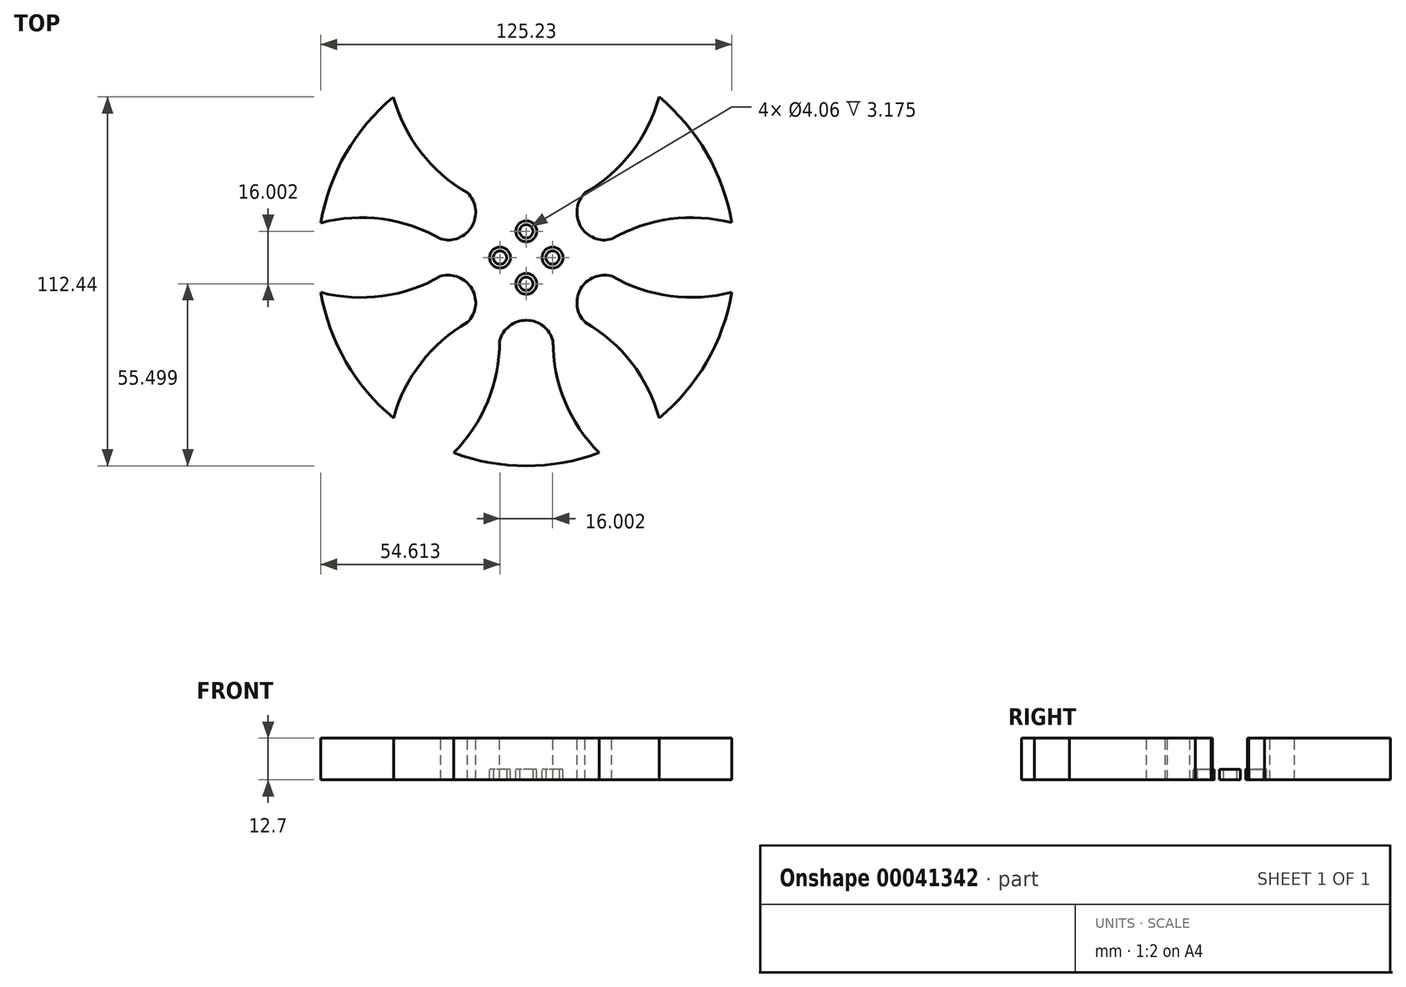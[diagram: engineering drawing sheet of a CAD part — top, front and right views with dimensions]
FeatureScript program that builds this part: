
annotation { "Feature Type Name" : "Feature", "Feature Type Description" : "" }
export const myFeature = defineFeature(function(context is Context, id is Id, definition is map)
    precondition{}
    {
        {
            var Q0;
            Q0=qCreatedBy(makeId("Top.planeOp"),FACE);
            var sketch = newSketch(context, id + "F0", { "sketchPlane" : qUnion([Q0])});
            skCircle(sketch, "E0", {"center": v(-620.67, 147.96) * mm, "radius": 63.5 * mm});
            skCircle(sketch, "E1", {"center": v(-620.67, 147.96) * mm, "radius": 4.06 * mm});
            skCircle(sketch, "E2", {"center": v(-612.66, 147.96) * mm, "radius": 2.03 * mm});
            skCircle(sketch, "E3", {"center": v(-620.67, 155.96) * mm, "radius": 2.03 * mm});
            skCircle(sketch, "E4", {"center": v(-628.67, 147.96) * mm, "radius": 2.03 * mm});
            skCircle(sketch, "E5", {"center": v(-620.67, 139.96) * mm, "radius": 2.03 * mm});
            skCircle(sketch, "E6", {"center": v(-620.67, 147.96) * mm, "radius": 25.4 * mm});
            skSolve(sketch);
        }
        {
            var Q0;
            Q0=makeQuery(id+"F0.imprint","IMPRINT",FACE,{"disambiguationData":[TD([[makeQuery(id+"F0.imprint","IMPRINT",EDGE,{"derivedFrom":sQuery(id+"F0.wireOp",EDGE,"E0")}),1.0]])]});
            var Q1;
            Q1=makeQuery(id+"F0.imprint","IMPRINT",FACE,{"disambiguationData":[TD([[makeQuery(id+"F0.imprint","IMPRINT",EDGE,{"derivedFrom":sQuery(id+"F0.wireOp",EDGE,"E1")}),-1.0]])]});
            extrude(context, id + "F1", {"entities" : qUnion([Q0, Q1]), "depth" : 12.7 * mm});
        }
        {
            var Q0;
            Q0=makeQuery(id+"F1.opExtrude","CAP_FACE",FACE,{"disambiguationData":[OSD([sQuery(id+"F0.wireOp",EDGE,"E0"),sQuery(id+"F0.wireOp",EDGE,"E1"),sQuery(id+"F0.wireOp",EDGE,"E2"),sQuery(id+"F0.wireOp",EDGE,"E3"),sQuery(id+"F0.wireOp",EDGE,"E4"),sQuery(id+"F0.wireOp",EDGE,"E5")])],"isStart":false});
            var sketch = newSketch(context, id + "F2", { "sketchPlane" : qUnion([Q0])});
            skCircle(sketch, "E7", {"center": v(-620.67, 155.96) * mm, "radius": 3.18 * mm});
            skCircle(sketch, "E8", {"center": v(-612.66, 147.96) * mm, "radius": 3.18 * mm});
            skCircle(sketch, "E9", {"center": v(-620.67, 139.96) * mm, "radius": 3.18 * mm});
            skCircle(sketch, "E10", {"center": v(-628.67, 147.96) * mm, "radius": 3.18 * mm});
            skLineSegment(sketch, "E11", {"start": v(-620.67, 155.96) * mm, "end": v(-620.67, 167.07) * mm});
            skArc(sketch, "E12", {"start": v(-598.54, 207.48) * mm, "mid": v(-608.9, 191.8) * mm, "end": v(-612.54, 173.36) * mm});
            skArc(sketch, "E13.MirrorCS", {"start": v(-642.82, 207.47) * mm, "mid": v(-632.44, 191.8) * mm, "end": v(-628.8, 173.36) * mm});
            skArc(sketch, "E14", {"start": v(-628.8, 173.36) * mm, "mid": v(-620.67, 167.07) * mm, "end": v(-612.54, 173.36) * mm});
            skPoint(sketch, "E15.orphan", {"position": v(-620.67, 211.46) * mm});
            skPoint(sketch, "E16.trimOffspring.start.orphan", {"position": v(-620.67, 173.36) * mm});
            skArc(sketch, "E17.1.0", {"start": v(-683.28, 158.53) * mm, "mid": v(-664.52, 159.69) * mm, "end": v(-646.73, 153.62) * mm});
            skArc(sketch, "E17.1.1", {"start": v(-646.73, 153.62) * mm, "mid": v(-637.21, 157.51) * mm, "end": v(-638.6, 167.7) * mm});
            skArc(sketch, "E17.1.2", {"start": v(-661.15, 196.88) * mm, "mid": v(-652.76, 180.06) * mm, "end": v(-638.6, 167.7) * mm});
            skArc(sketch, "E17.2.0", {"start": v(-661.12, 99.02) * mm, "mid": v(-652.75, 115.84) * mm, "end": v(-638.6, 128.22) * mm});
            skArc(sketch, "E17.2.1", {"start": v(-638.6, 128.22) * mm, "mid": v(-637.21, 138.4) * mm, "end": v(-646.73, 142.3) * mm});
            skArc(sketch, "E17.2.2", {"start": v(-683.28, 137.36) * mm, "mid": v(-664.51, 136.22) * mm, "end": v(-646.73, 142.3) * mm});
            skArc(sketch, "E17.3.0", {"start": v(-598.51, 88.45) * mm, "mid": v(-608.9, 104.12) * mm, "end": v(-612.54, 122.56) * mm});
            skArc(sketch, "E17.3.1", {"start": v(-612.54, 122.56) * mm, "mid": v(-620.67, 128.85) * mm, "end": v(-628.8, 122.56) * mm});
            skArc(sketch, "E17.3.2", {"start": v(-642.8, 88.44) * mm, "mid": v(-632.42, 104.12) * mm, "end": v(-628.8, 122.56) * mm});
            skArc(sketch, "E17.4.0", {"start": v(-558.05, 137.4) * mm, "mid": v(-576.81, 136.23) * mm, "end": v(-594.6, 142.3) * mm});
            skArc(sketch, "E17.4.1", {"start": v(-594.6, 142.3) * mm, "mid": v(-604.12, 138.4) * mm, "end": v(-602.73, 128.22) * mm});
            skArc(sketch, "E17.4.2", {"start": v(-580.18, 99.04) * mm, "mid": v(-588.58, 115.86) * mm, "end": v(-602.73, 128.22) * mm});
            skArc(sketch, "E17.5.0", {"start": v(-580.2, 196.9) * mm, "mid": v(-588.58, 180.07) * mm, "end": v(-602.73, 167.7) * mm});
            skArc(sketch, "E17.5.1", {"start": v(-602.73, 167.7) * mm, "mid": v(-604.12, 157.51) * mm, "end": v(-594.6, 153.62) * mm});
            skArc(sketch, "E17.5.2", {"start": v(-558.06, 158.56) * mm, "mid": v(-576.82, 159.7) * mm, "end": v(-594.6, 153.62) * mm});
            skPoint(sketch, "E17.center", {"position": v(-620.67, 147.96) * mm});
            skSolve(sketch);
        }
        {
            var Q0;
            Q0=makeQuery(id+"F2.imprint","IMPRINT",FACE,{"disambiguationData":[TD([[makeQuery(id+"F2.imprint","IMPRINT",EDGE,{"derivedFrom":sQuery(id+"F2.wireOp",EDGE,"E10")}),1.0]])]});
            var Q1;
            Q1=makeQuery(id+"F2.imprint","IMPRINT",FACE,{"disambiguationData":[TD([[makeQuery(id+"F2.imprint","IMPRINT",EDGE,{"derivedFrom":sQuery(id+"F2.wireOp",EDGE,"E7")}),1.0]])]});
            var Q2;
            Q2=makeQuery(id+"F2.imprint","IMPRINT",FACE,{"disambiguationData":[TD([[makeQuery(id+"F2.imprint","IMPRINT",EDGE,{"derivedFrom":sQuery(id+"F2.wireOp",EDGE,"E8")}),1.0]])]});
            var Q3;
            Q3=makeQuery(id+"F2.imprint","IMPRINT",FACE,{"disambiguationData":[TD([[makeQuery(id+"F2.imprint","IMPRINT",EDGE,{"derivedFrom":sQuery(id+"F2.wireOp",EDGE,"E9")}),1.0]])]});
            extrude(context, id + "F3", {"entities" : qUnion([Q0, Q1, Q2, Q3]), "operationType" : NewBodyOperationType.REMOVE, "oppositeDirection" : true, "depth" : 9.52 * mm});
        }
        {
            var Q0;
            {var subQ2=sQuery(id+"F2.wireOp",EDGE,"E12");Q0=makeQuery(id+"F2.imprint","IMPRINT",FACE,{"disambiguationData":[TD([[makeQuery(id+"F2.imprint","IMPRINT",EDGE,{"derivedFrom":subQ2}),-1.0]])]});}
            var Q1;
            {var subQ0=sQuery(id+"F2.wireOp",EDGE,"E17.1.0");Q1=makeQuery(id+"F2.imprint","IMPRINT",FACE,{"disambiguationData":[TD([[makeQuery(id+"F2.imprint","IMPRINT",EDGE,{"derivedFrom":subQ0}),1.0]])]});}
            var Q2;
            {var subQ0=sQuery(id+"F2.wireOp",EDGE,"E17.2.0");Q2=makeQuery(id+"F2.imprint","IMPRINT",FACE,{"disambiguationData":[TD([[makeQuery(id+"F2.imprint","IMPRINT",EDGE,{"derivedFrom":subQ0}),1.0]])]});}
            var Q3;
            {var subQ0=sQuery(id+"F2.wireOp",EDGE,"E17.3.0");Q3=makeQuery(id+"F2.imprint","IMPRINT",FACE,{"disambiguationData":[TD([[makeQuery(id+"F2.imprint","IMPRINT",EDGE,{"derivedFrom":subQ0}),1.0]])]});}
            var Q4;
            {var subQ0=sQuery(id+"F2.wireOp",EDGE,"E17.4.0");Q4=makeQuery(id+"F2.imprint","IMPRINT",FACE,{"disambiguationData":[TD([[makeQuery(id+"F2.imprint","IMPRINT",EDGE,{"derivedFrom":subQ0}),1.0]])]});}
            var Q5;
            {var subQ0=sQuery(id+"F2.wireOp",EDGE,"E17.5.0");Q5=makeQuery(id+"F2.imprint","IMPRINT",FACE,{"disambiguationData":[TD([[makeQuery(id+"F2.imprint","IMPRINT",EDGE,{"derivedFrom":subQ0}),1.0]])]});}
            extrude(context, id + "F4", {"entities" : qUnion([Q0, Q1, Q2, Q3, Q4, Q5]), "operationType" : NewBodyOperationType.REMOVE, "oppositeDirection" : true, "depth" : 12.7 * mm});
        }
    });
